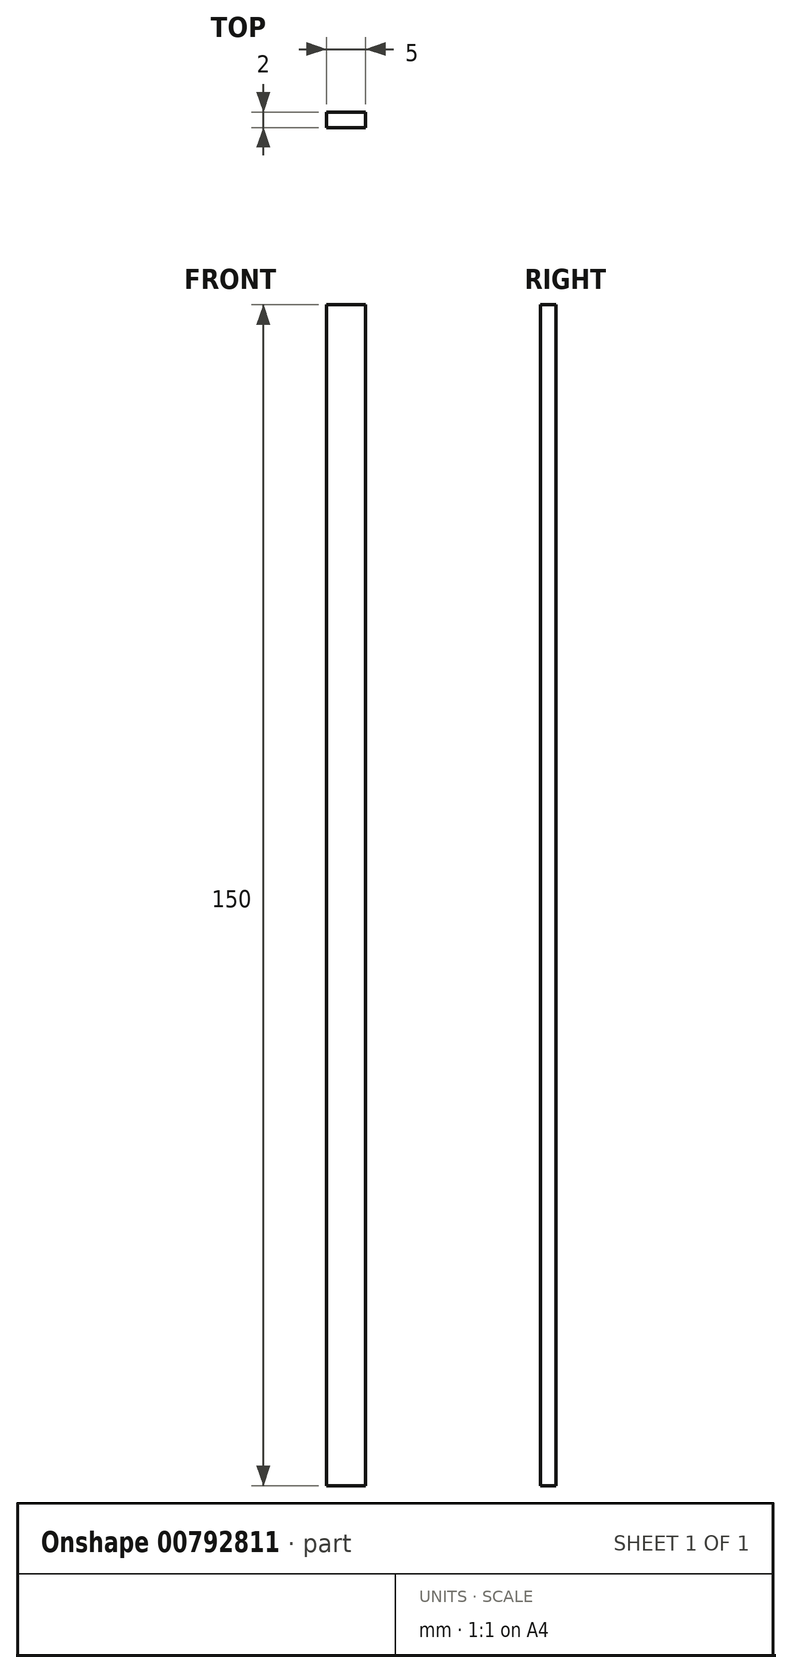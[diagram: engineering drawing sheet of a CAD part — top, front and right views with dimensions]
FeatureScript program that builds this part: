
annotation { "Feature Type Name" : "Feature", "Feature Type Description" : "" }
export const myFeature = defineFeature(function(context is Context, id is Id, definition is map)
    precondition{}
    {
        {
            var Q0;
            Q0=qCreatedBy(makeId("Top.planeOp"),FACE);
            var sketch = newSketch(context, id + "F0", { "sketchPlane" : qUnion([Q0])});
            skLineSegment(sketch, "E0.bottom", {"start": v(0, 0) * mm, "end": v(5, 0) * mm});
            skLineSegment(sketch, "E0.top", {"start": v(0, 2) * mm, "end": v(5, 2) * mm});
            skLineSegment(sketch, "E0.left", {"start": v(0, 0) * mm, "end": v(0, 2) * mm});
            skLineSegment(sketch, "E0.right", {"start": v(5, 0) * mm, "end": v(5, 2) * mm});
            skSolve(sketch);
        }
        {
            var Q0;
            Q0 = qSketchRegion(id + "F0", true);
            extrude(context, id + "F1", {"entities" : qUnion([Q0]), "depth" : 150 * mm, "offsetDistance" : 25 * mm});
        }
    });
